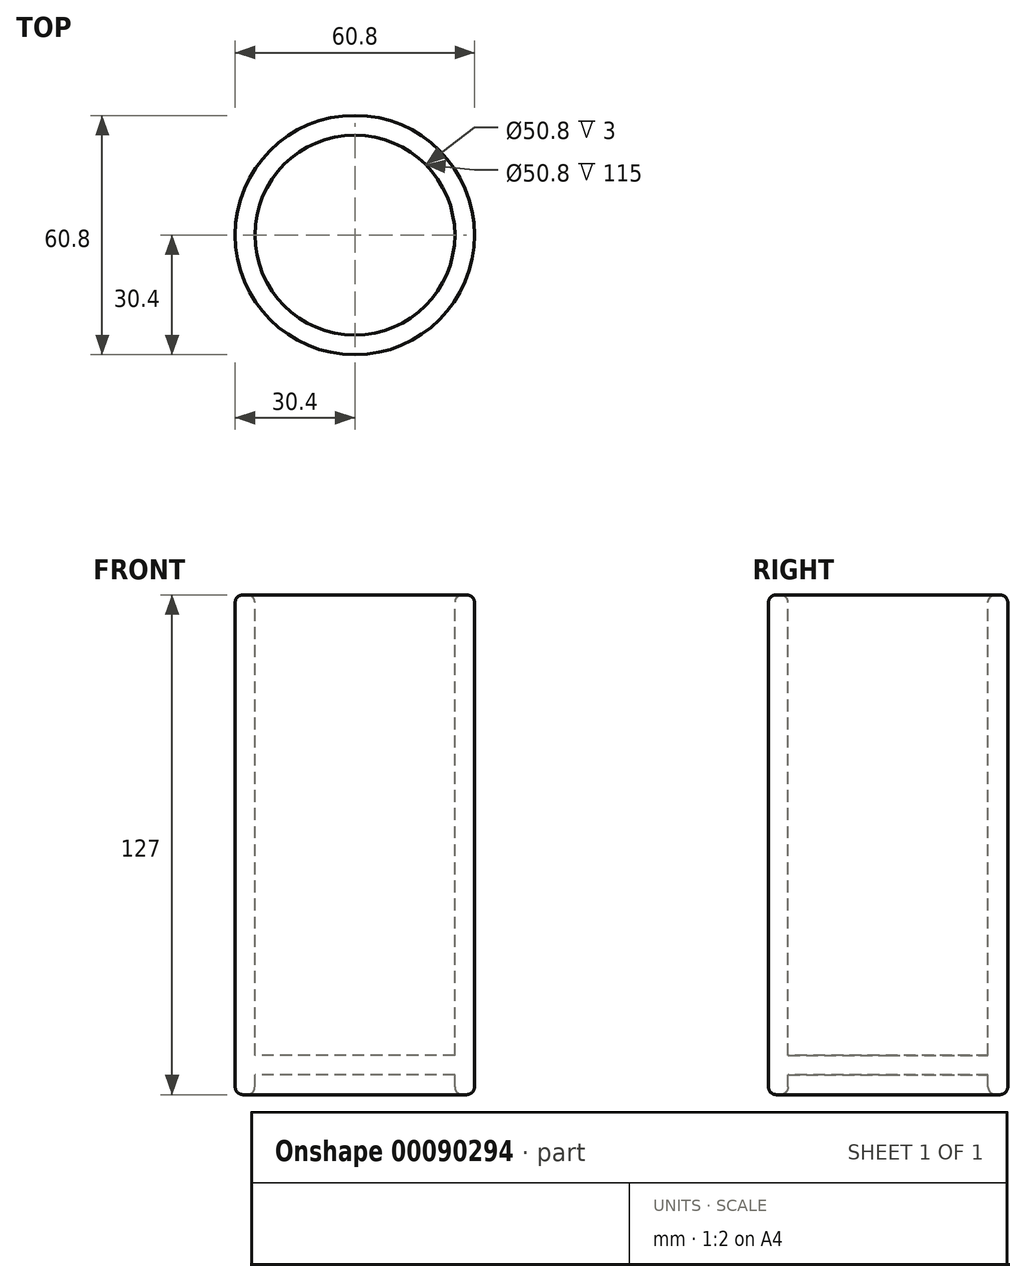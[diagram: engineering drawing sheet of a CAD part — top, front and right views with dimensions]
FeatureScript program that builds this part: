
annotation { "Feature Type Name" : "Feature", "Feature Type Description" : "" }
export const myFeature = defineFeature(function(context is Context, id is Id, definition is map)
    precondition{}
    {
        {
            var Q0;
            Q0=qCreatedBy(makeId("Front.planeOp"),FACE);
            var sketch = newSketch(context, id + "F0", { "sketchPlane" : qUnion([Q0])});
            skLineSegment(sketch, "E0", {"start": v(0, 73.57) * mm, "end": v(0, -46.84) * mm, "construction": true});
            skSolve(sketch);
        }
        {
            var Q0;
            Q0=qCreatedBy(makeId("Front.planeOp"),FACE);
            var sketch = newSketch(context, id + "F1", { "sketchPlane" : qUnion([Q0])});
            skLineSegment(sketch, "E1", {"start": v(0, 0) * mm, "end": v(25.4, 0) * mm});
            skLineSegment(sketch, "E2", {"start": v(25.4, 0) * mm, "end": v(25.4, 117) * mm});
            skLineSegment(sketch, "E3", {"start": v(25.4, 117) * mm, "end": v(30.4, 117) * mm});
            skLineSegment(sketch, "E4", {"start": v(30.4, 117) * mm, "end": v(30.4, -10) * mm});
            skLineSegment(sketch, "E5", {"start": v(30.4, -10) * mm, "end": v(25.4, -10) * mm});
            skLineSegment(sketch, "E6", {"start": v(25.4, -10) * mm, "end": v(25.4, -5) * mm});
            skLineSegment(sketch, "E7", {"start": v(25.4, -5) * mm, "end": v(0, -5) * mm});
            skLineSegment(sketch, "E8", {"start": v(0, -5) * mm, "end": v(0, 0) * mm});
            skSolve(sketch);
        }
        {
            var Q0;
            Q0=makeQuery(id+"F1.imprint","IMPRINT",FACE,{"disambiguationData":[TD([[makeQuery(id+"F1.imprint","IMPRINT",EDGE,{"derivedFrom":sQuery(id+"F1.wireOp",EDGE,"E1")}),-1.0]])]});
            var Q1;
            Q1=sQuery(id+"F0.wireOp",EDGE,"E0");
            revolve(context, id + "F2", {"entities" : qUnion([Q0]), "axis" : qUnion([Q1]), "revolveType" : RevolveType.FULL});
        }
        {
            var Q0;
            Q0=makeQuery(id+"F2.opRevolve","SWEPT_FACE",FACE,{"disambiguationData":[OSD([sQuery(id+"F1.wireOp",EDGE,"E3")])]});
            fillet(context, id + "F3", {"entities" : qUnion([Q0]), "radius" : 2 * mm, "tangentPropagation" : true, "allowEdgeOverflow" : false});
        }
        {
            var Q0;
            Q0=makeQuery(id+"F2.opRevolve","SWEPT_FACE",FACE,{"disambiguationData":[OSD([sQuery(id+"F1.wireOp",EDGE,"E5")])]});
            fillet(context, id + "F4", {"entities" : qUnion([Q0]), "radius" : 2 * mm, "tangentPropagation" : true, "allowEdgeOverflow" : false});
        }
    });
